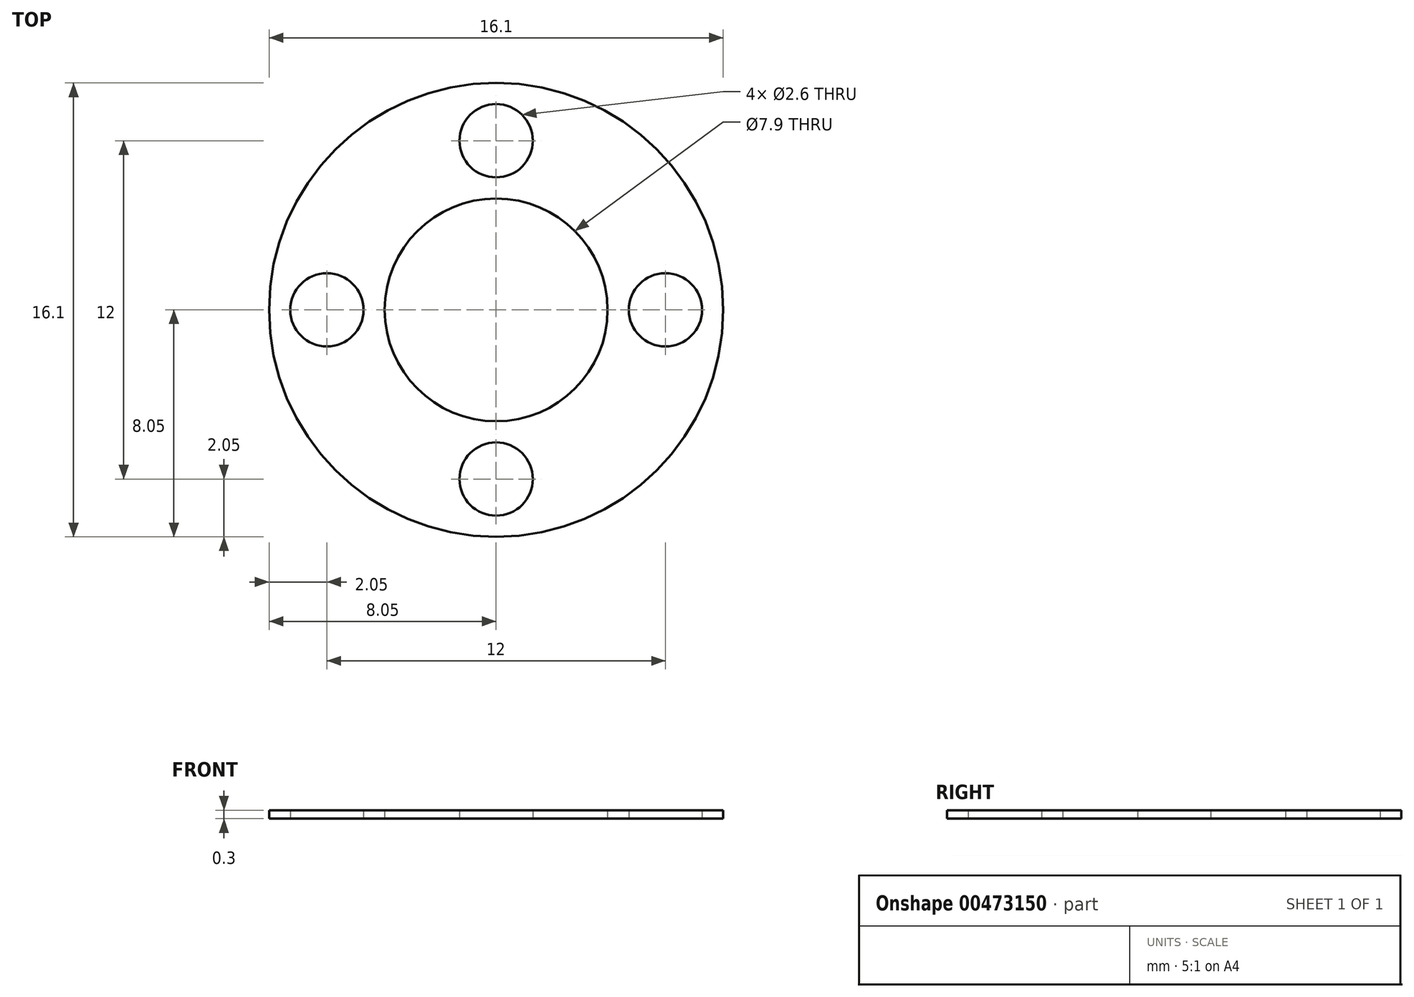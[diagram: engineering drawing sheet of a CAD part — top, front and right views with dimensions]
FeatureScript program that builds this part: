
annotation { "Feature Type Name" : "Feature", "Feature Type Description" : "" }
export const myFeature = defineFeature(function(context is Context, id is Id, definition is map)
    precondition{}
    {
        {
            var Q0;
            Q0=qCreatedBy(makeId("Top.planeOp"),FACE);
            var sketch = newSketch(context, id + "F0", { "sketchPlane" : qUnion([Q0])});
            skCircle(sketch, "E0", {"center": v(-6, 0) * mm, "radius": 1.3 * mm});
            skCircle(sketch, "E1", {"center": v(0, 6) * mm, "radius": 1.3 * mm});
            skCircle(sketch, "E2", {"center": v(6, 0) * mm, "radius": 1.3 * mm});
            skCircle(sketch, "E3", {"center": v(0, -6) * mm, "radius": 1.3 * mm});
            skLineSegment(sketch, "E4", {"start": v(-6, 0) * mm, "end": v(6, 0) * mm});
            skLineSegment(sketch, "E5", {"start": v(0, 6) * mm, "end": v(0, -6) * mm});
            skCircle(sketch, "E6", {"center": v(0, 0) * mm, "radius": 8.05 * mm});
            skCircle(sketch, "E7", {"center": v(0, 0) * mm, "radius": 3.95 * mm});
            skSolve(sketch);
        }
        {
            var Q0;
            Q0=makeQuery(id+"F0.imprint","IMPRINT",FACE,{"disambiguationData":[TD([[makeQuery(id+"F0.imprint","IMPRINT",EDGE,{"derivedFrom":sQuery(id+"F0.wireOp",EDGE,"E0")}),-1.0]])]});
            extrude(context, id + "F1", {"entities" : qUnion([Q0]), "depth" : 0.3 * mm});
        }
    });
